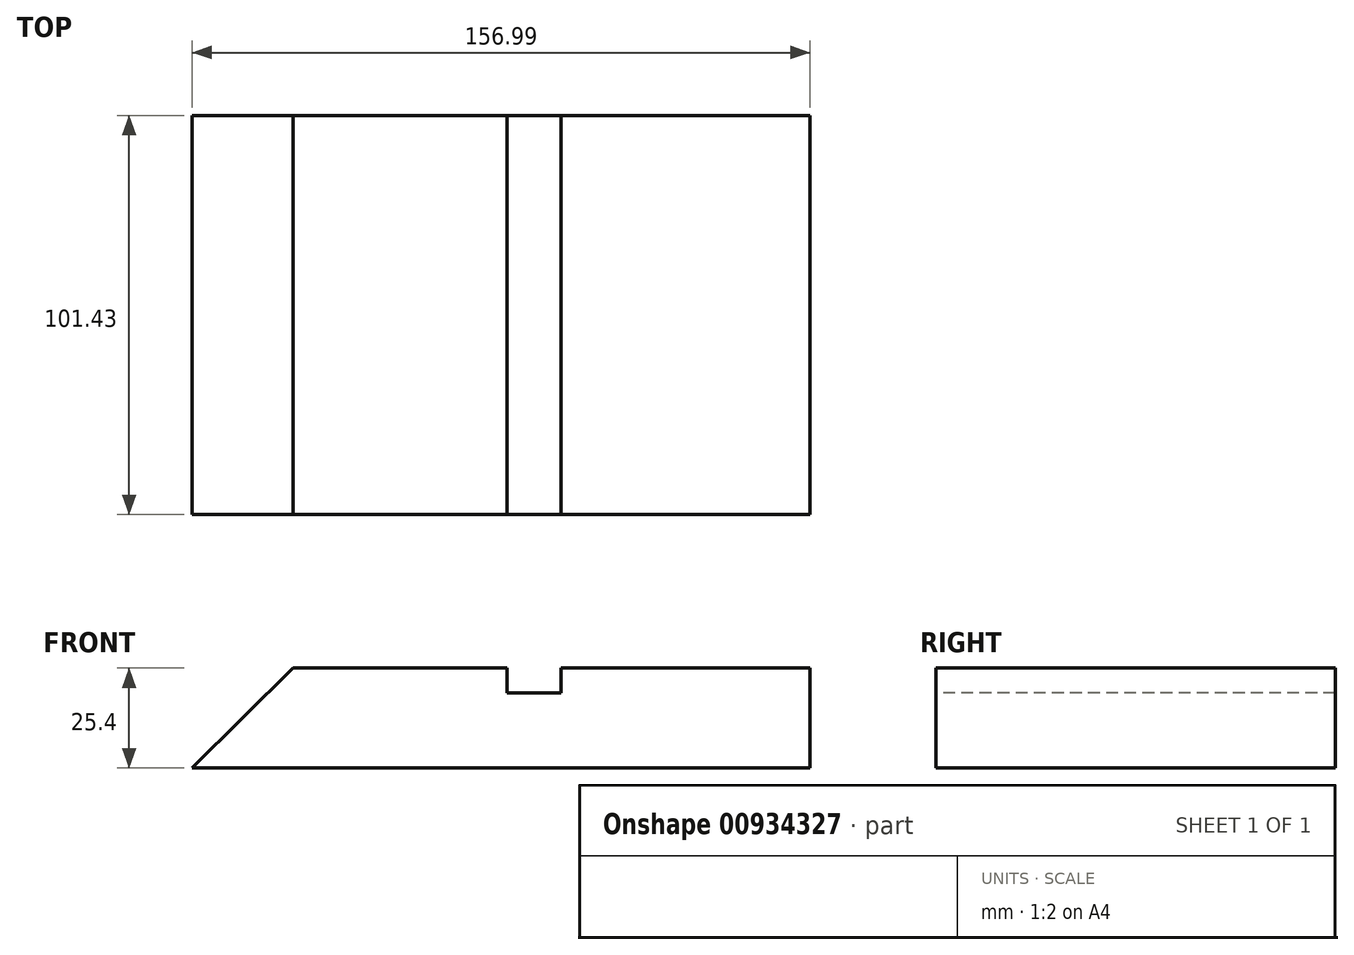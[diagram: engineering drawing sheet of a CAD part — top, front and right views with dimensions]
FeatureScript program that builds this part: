
annotation { "Feature Type Name" : "Feature", "Feature Type Description" : "" }
export const myFeature = defineFeature(function(context is Context, id is Id, definition is map)
    precondition{}
    {
        {
            var Q0;
            Q0=qCreatedBy(makeId("Top.planeOp"),FACE);
            var sketch = newSketch(context, id + "F0", { "sketchPlane" : qUnion([Q0])});
            skLineSegment(sketch, "E0.bottom", {"start": v(76.99, -47.42) * mm, "end": v(-80, -47.42) * mm});
            skLineSegment(sketch, "E0.top", {"start": v(76.99, 54.01) * mm, "end": v(-80, 54.01) * mm});
            skLineSegment(sketch, "E0.left", {"start": v(76.99, -47.42) * mm, "end": v(76.99, 54.01) * mm});
            skLineSegment(sketch, "E0.right", {"start": v(-80, -47.42) * mm, "end": v(-80, 54.01) * mm});
            skSolve(sketch);
        }
        {
            var Q0;
            Q0=makeQuery(id+"F0.imprint","IMPRINT",FACE,{"disambiguationData":[TD([[makeQuery(id+"F0.imprint","IMPRINT",EDGE,{"derivedFrom":sQuery(id+"F0.wireOp",EDGE,"E0.bottom")}),-1.0]])]});
            extrude(context, id + "F1", {"entities" : qUnion([Q0]), "depth" : 25.4 * mm, "offsetDistance" : 25.4 * mm});
        }
        {
            var Q0;
            Q0=makeQuery(id+"F1.opExtrude","SWEPT_FACE",FACE,{"disambiguationData":[OSD([sQuery(id+"F0.wireOp",EDGE,"E0.bottom")])]});
            var sketch = newSketch(context, id + "F2", { "sketchPlane" : qUnion([Q0])});
            skLineSegment(sketch, "E1", {"start": v(-80, 0) * mm, "end": v(-54.33, 25.4) * mm});
            skSolve(sketch);
        }
        {
            var Q0;
            {var subQ0=sQuery(id+"F2.wireOp",EDGE,"E1");Q0=makeQuery(id+"F2.imprint","IMPRINT",FACE,{"disambiguationData":[TD([[makeQuery(id+"F2.imprint","IMPRINT",EDGE,{"derivedFrom":subQ0}),1.0]])]});}
            var Q1;
            Q1=sQuery(id+"F2.wireOp",EDGE,"E1");
            extrude(context, id + "F3", {"entities" : qUnion([Q0]), "operationType" : NewBodyOperationType.REMOVE, "surfaceEntities" : qUnion([Q1]), "oppositeDirection" : true, "depth" : 127.82 * mm, "offsetDistance" : 25.4 * mm});
        }
        {
            var Q0;
            Q0=makeQuery(id+"F1.opExtrude","SWEPT_FACE",FACE,{"disambiguationData":[OSD([sQuery(id+"F0.wireOp",EDGE,"E0.bottom")])]});
            var sketch = newSketch(context, id + "F4", { "sketchPlane" : qUnion([Q0])});
            skLineSegment(sketch, "E2.bottom", {"start": v(13.77, 25.4) * mm, "end": v(0, 25.4) * mm});
            skLineSegment(sketch, "E2.top", {"start": v(13.77, 19.13) * mm, "end": v(0, 19.13) * mm});
            skLineSegment(sketch, "E2.left", {"start": v(13.77, 25.4) * mm, "end": v(13.77, 19.13) * mm});
            skLineSegment(sketch, "E2.right", {"start": v(0, 25.4) * mm, "end": v(0, 19.13) * mm});
            skSolve(sketch);
        }
        {
            var Q0;
            Q0=makeQuery(id+"F4.imprint","IMPRINT",FACE,{"disambiguationData":[TD([[makeQuery(id+"F4.imprint","IMPRINT",EDGE,{"derivedFrom":sQuery(id+"F4.wireOp",EDGE,"E2.bottom")}),1.0]])]});
            var Q1;
            Q1=sQuery(id+"F4.wireOp",EDGE,"E2.top");
            var Q2;
            Q2=sQuery(id+"F4.wireOp",EDGE,"E2.bottom");
            var Q3;
            Q3=sQuery(id+"F4.wireOp",EDGE,"E2.right");
            var Q4;
            Q4=sQuery(id+"F4.wireOp",EDGE,"E2.left");
            extrude(context, id + "F5", {"entities" : qUnion([Q0]), "operationType" : NewBodyOperationType.REMOVE, "surfaceEntities" : qUnion([Q1, Q2, Q3, Q4]), "oppositeDirection" : true, "depth" : 157.06 * mm, "offsetDistance" : 25.4 * mm});
        }
    });
